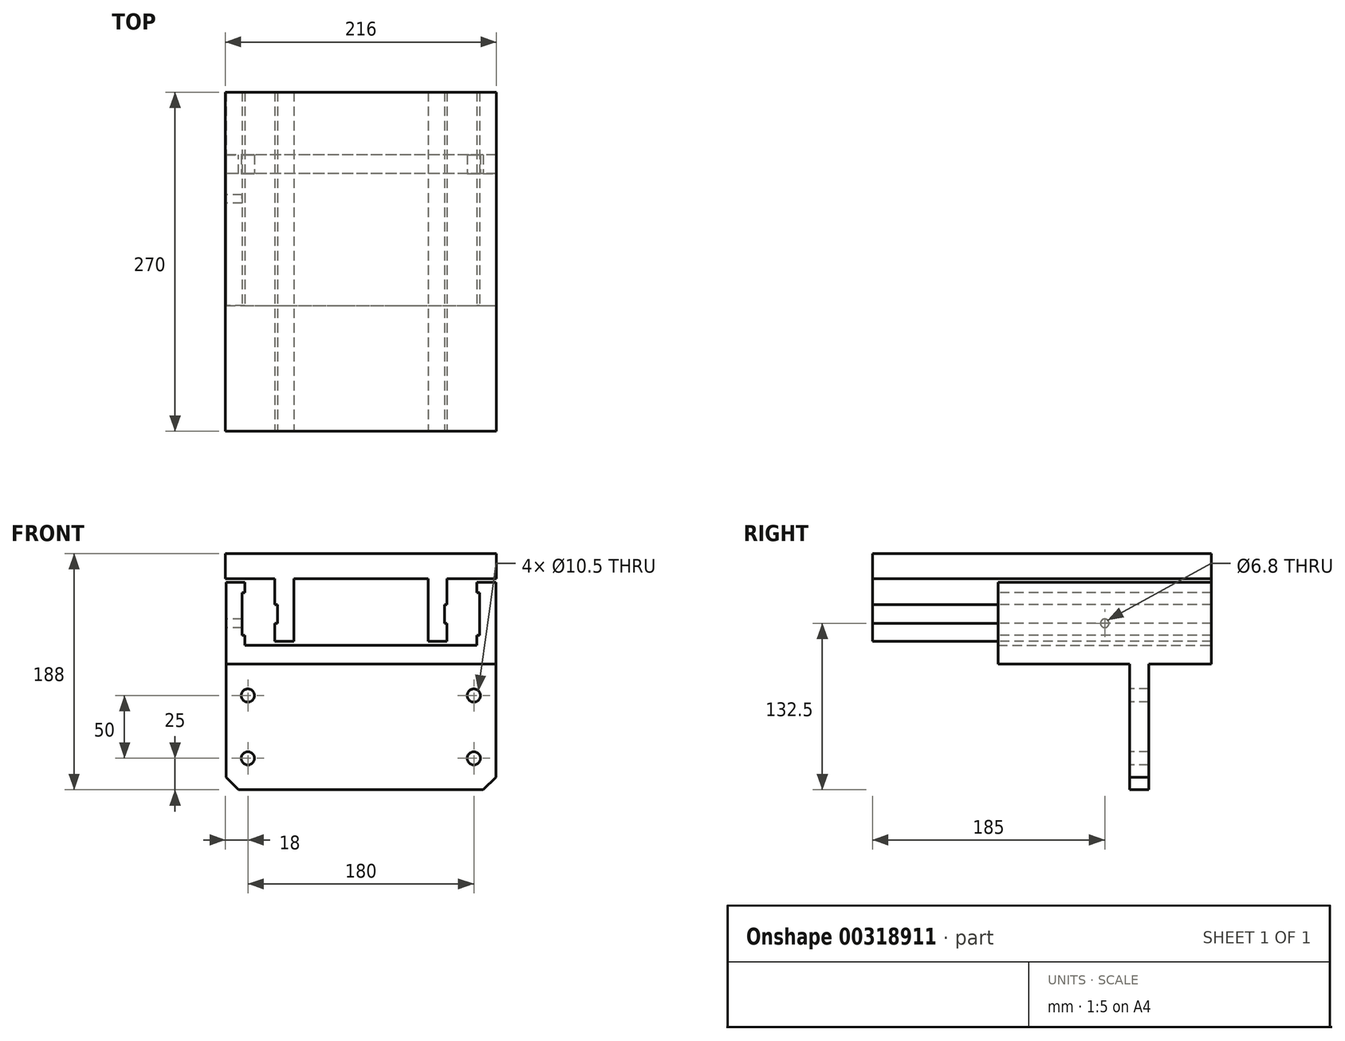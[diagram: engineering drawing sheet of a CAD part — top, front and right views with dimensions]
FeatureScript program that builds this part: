
annotation { "Feature Type Name" : "Feature", "Feature Type Description" : "" }
export const myFeature = defineFeature(function(context is Context, id is Id, definition is map)
    precondition{}
    {
        {
            var Q0;
            Q0=qCreatedBy(makeId("Front.planeOp"),FACE);
            var sketch = newSketch(context, id + "F0", { "sketchPlane" : qUnion([Q0])});
            skLineSegment(sketch, "E0.bottom", {"start": v(107.5, -50) * mm, "end": v(-107.5, -50) * mm});
            skLineSegment(sketch, "E0.top", {"start": v(107.5, 50) * mm, "end": v(-107.5, 50) * mm});
            skLineSegment(sketch, "E0.left", {"start": v(107.5, -50) * mm, "end": v(107.5, 50) * mm});
            skLineSegment(sketch, "E0.right", {"start": v(-107.5, -50) * mm, "end": v(-107.5, 50) * mm});
            skPoint(sketch, "E0.middle", {"position": v(0, 0) * mm});
            skSolve(sketch);
        }
        {
            var Q0;
            Q0=qCreatedBy(makeId("Right.planeOp"),FACE);
            cPlane(context, id + "F1", {"entities" : qUnion([Q0]), "cplaneType" : CPlaneType.OFFSET, "offset" : 107.5 * mm, "width" : 150 * mm, "height" : 150 * mm});
        }
        {
            var Q0;
            Q0=qCreatedBy(id+"F1.planeOp",FACE);
            var sketch = newSketch(context, id + "F2", { "sketchPlane" : qUnion([Q0])});
            skLineSegment(sketch, "E1", {"start": v(0, 0) * mm, "end": v(0, 65) * mm, "construction": true});
            skLineSegment(sketch, "E2", {"start": v(0, 65) * mm, "end": v(50, 65) * mm});
            skLineSegment(sketch, "E3", {"start": v(50, 65) * mm, "end": v(50, 50) * mm});
            skLineSegment(sketch, "E4", {"start": v(50, 50) * mm, "end": v(-120, 50) * mm});
            skLineSegment(sketch, "E5", {"start": v(-120, 50) * mm, "end": v(-120, 65) * mm});
            skLineSegment(sketch, "E6", {"start": v(-120, 65) * mm, "end": v(0, 65) * mm});
            skSolve(sketch);
        }
        {
            var Q0;
            Q0=makeQuery(id+"F0.imprint","IMPRINT",FACE,{"disambiguationData":[TD([[makeQuery(id+"F0.imprint","IMPRINT",EDGE,{"derivedFrom":sQuery(id+"F0.wireOp",EDGE,"E0.bottom")}),-1.0]])]});
            extrude(context, id + "F3", {"entities" : qUnion([Q0]), "depth" : 15 * mm});
        }
        {
            var Q0;
            Q0=makeQuery(id+"F2.imprint","IMPRINT",FACE,{"disambiguationData":[TD([[makeQuery(id+"F2.imprint","IMPRINT",EDGE,{"derivedFrom":sQuery(id+"F2.wireOp",EDGE,"E2")}),-1.0]])]});
            extrude(context, id + "F4", {"entities" : qUnion([Q0]), "operationType" : NewBodyOperationType.ADD, "oppositeDirection" : true, "depth" : 215 * mm});
        }
        {
            var Q0;
            Q0=qCreatedBy(id+"F1.planeOp",FACE);
            var sketch = newSketch(context, id + "F5", { "sketchPlane" : qUnion([Q0])});
            skLineSegment(sketch, "E7.0", {"start": v(-120, 65) * mm, "end": v(50, 65) * mm});
            skLineSegment(sketch, "E8", {"start": v(50, 65) * mm, "end": v(50, 115) * mm});
            skLineSegment(sketch, "E9", {"start": v(50, 115) * mm, "end": v(-120, 115) * mm});
            skLineSegment(sketch, "E10", {"start": v(-120, 115) * mm, "end": v(-120, 65) * mm});
            skSolve(sketch);
        }
        {
            var Q0;
            Q0=makeQuery(id+"F5.imprint","IMPRINT",FACE,{"disambiguationData":[TD([[makeQuery(id+"F5.imprint","IMPRINT",EDGE,{"derivedFrom":sQuery(id+"F5.wireOp",EDGE,"E7.0")}),1.0]])]});
            extrude(context, id + "F6", {"entities" : qUnion([Q0]), "operationType" : NewBodyOperationType.ADD, "oppositeDirection" : true, "depth" : 15 * mm});
        }
        {
            var Q0;
            Q0=qCreatedBy(id+"F1.planeOp",FACE);
            cPlane(context, id + "F7", {"entities" : qUnion([Q0]), "cplaneType" : CPlaneType.OFFSET, "offset" : 215 * mm, "oppositeDirection" : true, "width" : 150 * mm, "height" : 150 * mm});
        }
        {
            var Q0;
            Q0=qCreatedBy(id+"F7.planeOp",FACE);
            var sketch = newSketch(context, id + "F8", { "sketchPlane" : qUnion([Q0])});
            skLineSegment(sketch, "E11.0", {"start": v(-120, 50) * mm, "end": v(-120, 115) * mm});
            skLineSegment(sketch, "E12.0", {"start": v(50, 115) * mm, "end": v(-120, 115) * mm});
            skLineSegment(sketch, "E13.0", {"start": v(50, 115) * mm, "end": v(50, 50) * mm});
            skLineSegment(sketch, "E14", {"start": v(50, 50) * mm, "end": v(-120, 50) * mm});
            skSolve(sketch);
        }
        {
            var Q0;
            Q0=makeQuery(id+"F8.imprint","IMPRINT",FACE,{"disambiguationData":[TD([[makeQuery(id+"F8.imprint","IMPRINT",EDGE,{"derivedFrom":sQuery(id+"F8.wireOp",EDGE,"E11.0")}),-1.0]])]});
            extrude(context, id + "F9", {"entities" : qUnion([Q0]), "operationType" : NewBodyOperationType.ADD, "depth" : 15 * mm});
        }
        {
            var Q0;
            Q0=makeQuery(id+"F9.opExtrude","CAP_FACE",FACE,{"disambiguationData":[OSD([sQuery(id+"F8.wireOp",EDGE,"E11.0"),sQuery(id+"F8.wireOp",EDGE,"E12.0"),sQuery(id+"F8.wireOp",EDGE,"E13.0"),sQuery(id+"F8.wireOp",EDGE,"E14")])],"isStart":false});
            var sketch = newSketch(context, id + "F10", { "sketchPlane" : qUnion([Q0])});
            skLineSegment(sketch, "E15", {"start": v(-35, 65) * mm, "end": v(-35, 90) * mm, "construction": true});
            skPoint(sketch, "E15.startSnap0", {"position": v(-35, 65) * mm});
            skPoint(sketch, "E15.startSnap1", {"position": v(-35, 76.78) * mm});
            skLineSegment(sketch, "E16.bottom", {"start": v(50, 73) * mm, "end": v(-120, 73) * mm});
            skLineSegment(sketch, "E16.top", {"start": v(50, 107) * mm, "end": v(-120, 107) * mm});
            skLineSegment(sketch, "E16.left", {"start": v(50, 73) * mm, "end": v(50, 107) * mm});
            skLineSegment(sketch, "E16.right", {"start": v(-120, 73) * mm, "end": v(-120, 107) * mm});
            skPoint(sketch, "E16.middle", {"position": v(-35, 90) * mm});
            skPoint(sketch, "E17", {"position": v(-120, 65) * mm});
            skPoint(sketch, "E18", {"position": v(50, 65) * mm});
            skSolve(sketch);
        }
        {
            var Q0;
            Q0=makeQuery(id+"F6.opExtrude","CAP_FACE",FACE,{"disambiguationData":[OSD([sQuery(id+"F5.wireOp",EDGE,"E7.0"),sQuery(id+"F5.wireOp",EDGE,"E8"),sQuery(id+"F5.wireOp",EDGE,"E9"),sQuery(id+"F5.wireOp",EDGE,"E10")])],"isStart":false});
            var sketch = newSketch(context, id + "F11", { "sketchPlane" : qUnion([Q0])});
            skLineSegment(sketch, "E19.0", {"start": v(-50, 107) * mm, "end": v(120, 107) * mm});
            skLineSegment(sketch, "E20.0", {"start": v(-50, 73) * mm, "end": v(120, 73) * mm});
            skLineSegment(sketch, "E21.0", {"start": v(-50, 73) * mm, "end": v(-50, 107) * mm});
            skLineSegment(sketch, "E22.0", {"start": v(120, 73) * mm, "end": v(120, 107) * mm});
            skSolve(sketch);
        }
        {
            var Q0;
            Q0=makeQuery(id+"F10.imprint","IMPRINT",FACE,{"disambiguationData":[TD([[makeQuery(id+"F10.imprint","IMPRINT",EDGE,{"derivedFrom":sQuery(id+"F10.wireOp",EDGE,"E16.bottom")}),-1.0]])]});
            extrude(context, id + "F12", {"entities" : qUnion([Q0]), "operationType" : NewBodyOperationType.REMOVE, "oppositeDirection" : true, "depth" : 2 * mm});
        }
        {
            var Q0;
            Q0=makeQuery(id+"F11.imprint","IMPRINT",FACE,{"disambiguationData":[TD([[makeQuery(id+"F11.imprint","IMPRINT",EDGE,{"derivedFrom":sQuery(id+"F11.wireOp",EDGE,"E19.0")}),-1.0]])]});
            extrude(context, id + "F13", {"entities" : qUnion([Q0]), "operationType" : NewBodyOperationType.REMOVE, "oppositeDirection" : true, "depth" : 2 * mm});
        }
        {
            var Q0;
            Q0=makeQuery(id+"F3.opExtrude","CAP_FACE",FACE,{"disambiguationData":[OSD([sQuery(id+"F0.wireOp",EDGE,"E0.bottom"),sQuery(id+"F0.wireOp",EDGE,"E0.top"),sQuery(id+"F0.wireOp",EDGE,"E0.left"),sQuery(id+"F0.wireOp",EDGE,"E0.right")])],"isStart":false});
            var sketch = newSketch(context, id + "F14", { "sketchPlane" : qUnion([Q0])});
            skLineSegment(sketch, "E23.bottom", {"start": v(90, 25) * mm, "end": v(-90, 25) * mm, "construction": true});
            skLineSegment(sketch, "E23.top", {"start": v(90, -25) * mm, "end": v(-90, -25) * mm, "construction": true});
            skLineSegment(sketch, "E23.left", {"start": v(90, 25) * mm, "end": v(90, -25) * mm, "construction": true});
            skLineSegment(sketch, "E23.right", {"start": v(-90, 25) * mm, "end": v(-90, -25) * mm, "construction": true});
            skPoint(sketch, "E23.middle", {"position": v(0, 0) * mm});
            skPoint(sketch, "E24", {"position": v(-90, 25) * mm});
            skPoint(sketch, "E25", {"position": v(-90, -25) * mm});
            skPoint(sketch, "E26", {"position": v(90, 25) * mm});
            skPoint(sketch, "E27", {"position": v(90, -25) * mm});
            skSolve(sketch);
        }
        {
            var Q0;
            Q0=sQuery(id+"F14.wireOp",VERTEX,"E24");
            var Q1;
            Q1=sQuery(id+"F14.wireOp",VERTEX,"E25");
            var Q2;
            Q2=sQuery(id+"F14.wireOp",VERTEX,"E27");
            var Q3;
            Q3=sQuery(id+"F14.wireOp",VERTEX,"E26");
            var Q4;
            Q4=makeQuery(id+"F3.opExtrude","SWEPT_BODY",BODY,{"disambiguationData":[OSD([sQuery(id+"F0.wireOp",EDGE,"E0.bottom"),sQuery(id+"F0.wireOp",EDGE,"E0.top"),sQuery(id+"F0.wireOp",EDGE,"E0.left"),sQuery(id+"F0.wireOp",EDGE,"E0.right")])]});
            hole(context, id + "F15", {"style" : HoleStyle.SIMPLE, "endStyle" : HoleEndStyle.THROUGH, "standardTappedOrClearance" : lookupTablePath({ "standard" : "ISO", "fit" : "Close", "size" : "M10", "type" : "Clearance" }), "standardBlindInLast" : lookupTablePath({ "fit" : "Close", "standard" : "ISO", "size" : "M10", "type" : "Clearance" }), "holeDiameter" : 10.5 * mm, "tappedDepth" : 21.25 * mm, "tapClearance" : 3, "locations" : qUnion([Q0, Q1, Q2, Q3]), "scope" : qUnion([Q4])});
        }
        {
            var Q0;
            Q0=makeQuery(id+"F3.opExtrude","SWEPT_EDGE",EDGE,{"disambiguationData":[OSD([sQuery(id+"F0.wireOp",EDGE,"E0.bottom"),sQuery(id+"F0.wireOp",EDGE,"E0.left")])]});
            var Q1;
            Q1=makeQuery(id+"F3.opExtrude","SWEPT_EDGE",EDGE,{"disambiguationData":[OSD([sQuery(id+"F0.wireOp",EDGE,"E0.bottom"),sQuery(id+"F0.wireOp",EDGE,"E0.right")])]});
            chamfer(context, id + "F16", {"entities" : qUnion([Q0, Q1]), "width" : 10 * mm, "tangentPropagation" : true});
        }
        {
            var Q0;
            Q0=qCreatedBy(makeId("Top.planeOp"),FACE);
            cPlane(context, id + "F17", {"entities" : qUnion([Q0]), "cplaneType" : CPlaneType.OFFSET, "offset" : 118 * mm, "width" : 150 * mm, "height" : 150 * mm});
        }
        {
            var Q0;
            Q0=qCreatedBy(id+"F17.planeOp",FACE);
            var sketch = newSketch(context, id + "F18", { "sketchPlane" : qUnion([Q0])});
            skLineSegment(sketch, "E28.bottom", {"start": v(108, -220) * mm, "end": v(-108, -220) * mm});
            skLineSegment(sketch, "E28.top", {"start": v(108, 50) * mm, "end": v(-108, 50) * mm});
            skLineSegment(sketch, "E29", {"start": v(-108, 50) * mm, "end": v(-108, -220) * mm});
            skLineSegment(sketch, "E30", {"start": v(108, 50) * mm, "end": v(108, -220) * mm});
            skSolve(sketch);
        }
        {
            var Q0;
            Q0=makeQuery(id+"F18.imprint","IMPRINT",FACE,{"disambiguationData":[TD([[makeQuery(id+"F18.imprint","IMPRINT",EDGE,{"derivedFrom":sQuery(id+"F18.wireOp",EDGE,"E28.bottom")}),-1.0]])]});
            extrude(context, id + "F19", {"entities" : qUnion([Q0]), "depth" : 20 * mm});
        }
        {
            var Q0;
            Q0=makeQuery(id+"F12.boolean.opBoolean","COPY",FACE,{"derivedFrom":makeQuery(id+"F12.opExtrude","CAP_FACE",FACE,{"disambiguationData":[OSD([sQuery(id+"F10.wireOp",EDGE,"E16.bottom"),sQuery(id+"F10.wireOp",EDGE,"E16.top"),sQuery(id+"F10.wireOp",EDGE,"E16.left"),sQuery(id+"F10.wireOp",EDGE,"E16.right")])],"isStart":false})});
            cPlane(context, id + "F20", {"entities" : qUnion([Q0]), "cplaneType" : CPlaneType.OFFSET, "offset" : 26 * mm, "width" : 150 * mm, "height" : 150 * mm});
        }
        {
            var Q0;
            Q0=makeQuery(id+"F13.boolean.opBoolean","COPY",FACE,{"derivedFrom":makeQuery(id+"F13.opExtrude","CAP_FACE",FACE,{"disambiguationData":[OSD([sQuery(id+"F11.wireOp",EDGE,"E19.0"),sQuery(id+"F11.wireOp",EDGE,"E20.0"),sQuery(id+"F11.wireOp",EDGE,"E21.0"),sQuery(id+"F11.wireOp",EDGE,"E22.0")])],"isStart":false})});
            cPlane(context, id + "F21", {"entities" : qUnion([Q0]), "cplaneType" : CPlaneType.OFFSET, "offset" : 26 * mm, "width" : 150 * mm, "height" : 150 * mm});
        }
        {
            var Q0;
            Q0=qCreatedBy(id+"F20.planeOp",FACE);
            var sketch = newSketch(context, id + "F22", { "sketchPlane" : qUnion([Q0])});
            skLineSegment(sketch, "E31.0", {"start": v(50, 118) * mm, "end": v(-220, 118) * mm});
            skLineSegment(sketch, "E32", {"start": v(50, 118) * mm, "end": v(50, 68) * mm});
            skLineSegment(sketch, "E33", {"start": v(50, 68) * mm, "end": v(-220, 68) * mm});
            skLineSegment(sketch, "E34", {"start": v(-220, 118) * mm, "end": v(-220, 68) * mm});
            skSolve(sketch);
        }
        {
            var Q0;
            Q0=qCreatedBy(id+"F21.planeOp",FACE);
            var sketch = newSketch(context, id + "F23", { "sketchPlane" : qUnion([Q0])});
            skLineSegment(sketch, "E35.0", {"start": v(-50, 118) * mm, "end": v(-50, 68) * mm});
            skLineSegment(sketch, "E36.0", {"start": v(220, 118) * mm, "end": v(220, 68) * mm});
            skLineSegment(sketch, "E37.0", {"start": v(-50, 118) * mm, "end": v(220, 118) * mm});
            skLineSegment(sketch, "E38.0", {"start": v(-50, 68) * mm, "end": v(220, 68) * mm});
            skSolve(sketch);
        }
        {
            var Q0;
            Q0=makeQuery(id+"F22.imprint","IMPRINT",FACE,{"disambiguationData":[TD([[makeQuery(id+"F22.imprint","IMPRINT",EDGE,{"derivedFrom":sQuery(id+"F22.wireOp",EDGE,"E31.0")}),1.0]])]});
            extrude(context, id + "F24", {"entities" : qUnion([Q0]), "operationType" : NewBodyOperationType.ADD, "depth" : 15 * mm});
        }
        {
            var Q0;
            Q0=makeQuery(id+"F23.imprint","IMPRINT",FACE,{"disambiguationData":[TD([[makeQuery(id+"F23.imprint","IMPRINT",EDGE,{"derivedFrom":sQuery(id+"F23.wireOp",EDGE,"E35.0")}),1.0]])]});
            extrude(context, id + "F25", {"entities" : qUnion([Q0]), "operationType" : NewBodyOperationType.ADD, "depth" : 15 * mm});
        }
        {
            var Q0;
            Q0=makeQuery(id+"F23.imprint","IMPRINT",FACE,{"disambiguationData":[TD([[makeQuery(id+"F23.imprint","IMPRINT",EDGE,{"derivedFrom":sQuery(id+"F23.wireOp",EDGE,"E35.0")}),1.0]])]});
            var sketch = newSketch(context, id + "F26", { "sketchPlane" : qUnion([Q0])});
            skLineSegment(sketch, "E39.0", {"start": v(35, 65) * mm, "end": v(35, 90) * mm, "construction": true});
            skPoint(sketch, "E40.middle", {"position": v(35, 90) * mm});
            skLineSegment(sketch, "E41", {"start": v(35, 90) * mm, "end": v(85, 90) * mm, "construction": true});
            skLineSegment(sketch, "E42.bottom", {"start": v(-50, 82.5) * mm, "end": v(220, 82.5) * mm});
            skLineSegment(sketch, "E42.top", {"start": v(-50, 97.5) * mm, "end": v(220, 97.5) * mm});
            skLineSegment(sketch, "E42.left", {"start": v(-50, 82.5) * mm, "end": v(-50, 97.5) * mm});
            skLineSegment(sketch, "E42.right", {"start": v(220, 82.5) * mm, "end": v(220, 97.5) * mm});
            skPoint(sketch, "E42.middle", {"position": v(85, 90) * mm});
            skSolve(sketch);
        }
        {
            var Q0;
            Q0=qCreatedBy(id+"F20.planeOp",FACE);
            var sketch = newSketch(context, id + "F27", { "sketchPlane" : qUnion([Q0])});
            skLineSegment(sketch, "E43.0", {"start": v(50, 97.5) * mm, "end": v(-220, 97.5) * mm});
            skPoint(sketch, "E44.0", {"position": v(50, 90) * mm});
            skLineSegment(sketch, "E45.0", {"start": v(50, 82.5) * mm, "end": v(-220, 82.5) * mm});
            skLineSegment(sketch, "E46.0", {"start": v(-220, 82.5) * mm, "end": v(-220, 97.5) * mm});
            skLineSegment(sketch, "E47.0", {"start": v(50, 82.5) * mm, "end": v(50, 97.5) * mm});
            skSolve(sketch);
        }
        {
            var Q0;
            Q0=makeQuery(id+"F26.imprint","IMPRINT",FACE,{"disambiguationData":[TD([[makeQuery(id+"F26.imprint","IMPRINT",EDGE,{"derivedFrom":sQuery(id+"F26.wireOp",EDGE,"E42.bottom")}),1.0]])]});
            extrude(context, id + "F28", {"entities" : qUnion([Q0]), "operationType" : NewBodyOperationType.REMOVE, "depth" : 2 * mm});
        }
        {
            var Q0;
            Q0=makeQuery(id+"F27.imprint","IMPRINT",FACE,{"disambiguationData":[TD([[makeQuery(id+"F27.imprint","IMPRINT",EDGE,{"derivedFrom":sQuery(id+"F27.wireOp",EDGE,"E43.0")}),1.0]])]});
            extrude(context, id + "F29", {"entities" : qUnion([Q0]), "operationType" : NewBodyOperationType.REMOVE, "depth" : 2 * mm});
        }
        {
            var Q0;
            Q0=qCreatedBy(id+"F7.planeOp",FACE);
            var sketch = newSketch(context, id + "F30", { "sketchPlane" : qUnion([Q0])});
            skPoint(sketch, "E48", {"position": v(-35, 82.5) * mm});
            skSolve(sketch);
        }
        {
            var Q0;
            Q0=sQuery(id+"F30.wireOp",VERTEX,"E48");
            var Q1;
            Q1=makeQuery(id+"F3.opExtrude","SWEPT_BODY",BODY,{"disambiguationData":[OSD([sQuery(id+"F0.wireOp",EDGE,"E0.bottom"),sQuery(id+"F0.wireOp",EDGE,"E0.top"),sQuery(id+"F0.wireOp",EDGE,"E0.left"),sQuery(id+"F0.wireOp",EDGE,"E0.right")])]});
            hole(context, id + "F31", {"style" : HoleStyle.SIMPLE, "endStyle" : HoleEndStyle.BLIND, "oppositeDirection" : true, "standardTappedOrClearance" : lookupTablePath({ "standard" : "ISO", "engagement" : "75%", "pitch" : "1.25 mm", "size" : "M8", "type" : "Tapped" }), "standardBlindInLast" : lookupTablePath({ "standard" : "ISO", "engagement" : "75%", "pitch" : "1.25 mm", "size" : "M8", "type" : "Tapped" }), "holeDiameter" : 6.8 * mm, "showTappedDepth" : true, "holeDepth" : 25 * mm, "tappedDepth" : 21.25 * mm, "tapClearance" : 3, "locations" : qUnion([Q0]), "scope" : qUnion([Q1]), "majorDiameter" : 8 * mm});
        }
    });
